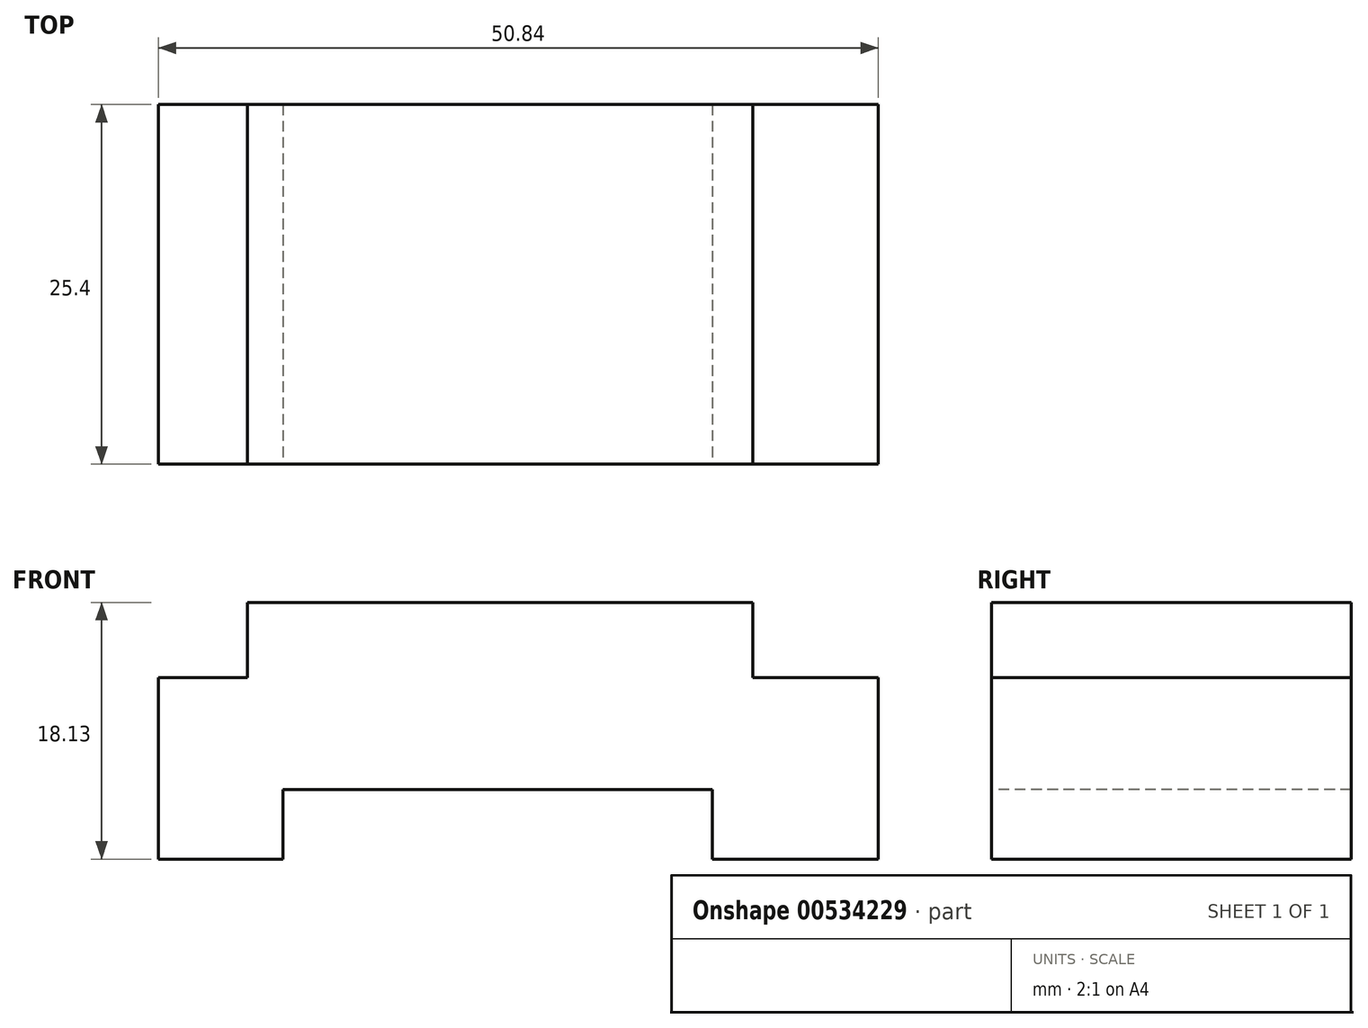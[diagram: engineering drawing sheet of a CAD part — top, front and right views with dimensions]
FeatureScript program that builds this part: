
annotation { "Feature Type Name" : "Feature", "Feature Type Description" : "" }
export const myFeature = defineFeature(function(context is Context, id is Id, definition is map)
    precondition{}
    {
        {
            var Q0;
            Q0=qCreatedBy(makeId("Front.planeOp"),FACE);
            var sketch = newSketch(context, id + "F0", { "sketchPlane" : qUnion([Q0])});
            skLineSegment(sketch, "E0", {"start": v(0, 0) * mm, "end": v(-50.84, 0) * mm});
            skLineSegment(sketch, "E1", {"start": v(-50.84, 0) * mm, "end": v(-50.84, 12.8) * mm});
            skLineSegment(sketch, "E2", {"start": v(-50.84, 12.8) * mm, "end": v(-44.54, 12.8) * mm});
            skLineSegment(sketch, "E3", {"start": v(-44.54, 12.8) * mm, "end": v(-44.54, 18.13) * mm});
            skLineSegment(sketch, "E4", {"start": v(0, 0) * mm, "end": v(0, 12.8) * mm});
            skLineSegment(sketch, "E5", {"start": v(0, 12.8) * mm, "end": v(-8.87, 12.8) * mm});
            skLineSegment(sketch, "E6", {"start": v(-8.87, 12.8) * mm, "end": v(-8.87, 18.13) * mm});
            skLineSegment(sketch, "E7", {"start": v(-8.87, 18.13) * mm, "end": v(-44.54, 18.13) * mm});
            skSolve(sketch);
        }
        {
            var Q0;
            Q0=makeQuery(id+"F0.imprint","IMPRINT",FACE,{"disambiguationData":[TD([[makeQuery(id+"F0.imprint","IMPRINT",EDGE,{"derivedFrom":sQuery(id+"F0.wireOp",EDGE,"E0")}),-1.0]])]});
            extrude(context, id + "F1", {"entities" : qUnion([Q0]), "depth" : 25.4 * mm, "offsetDistance" : 25.4 * mm});
        }
        {
            var Q0;
            Q0=makeQuery(id+"F1.opExtrude","CAP_FACE",FACE,{"disambiguationData":[OSD([sQuery(id+"F0.wireOp",EDGE,"E0"),sQuery(id+"F0.wireOp",EDGE,"E1"),sQuery(id+"F0.wireOp",EDGE,"E2"),sQuery(id+"F0.wireOp",EDGE,"E3"),sQuery(id+"F0.wireOp",EDGE,"E4"),sQuery(id+"F0.wireOp",EDGE,"E5"),sQuery(id+"F0.wireOp",EDGE,"E6"),sQuery(id+"F0.wireOp",EDGE,"E7")])],"isStart":false});
            var sketch = newSketch(context, id + "F2", { "sketchPlane" : qUnion([Q0])});
            skLineSegment(sketch, "E8.bottom", {"start": v(-42.04, 0) * mm, "end": v(-11.72, 0) * mm});
            skLineSegment(sketch, "E8.top", {"start": v(-42.04, 4.92) * mm, "end": v(-11.72, 4.92) * mm});
            skLineSegment(sketch, "E8.left", {"start": v(-42.04, 0) * mm, "end": v(-42.04, 4.92) * mm});
            skLineSegment(sketch, "E8.right", {"start": v(-11.72, 0) * mm, "end": v(-11.72, 4.92) * mm});
            skSolve(sketch);
        }
        {
            var Q0;
            Q0=makeQuery(id+"F2.imprint","IMPRINT",FACE,{"disambiguationData":[TD([[makeQuery(id+"F2.imprint","IMPRINT",EDGE,{"derivedFrom":sQuery(id+"F2.wireOp",EDGE,"E8.bottom")}),-1.0]])]});
            extrude(context, id + "F3", {"entities" : qUnion([Q0]), "operationType" : NewBodyOperationType.REMOVE, "oppositeDirection" : true, "depth" : 25.4 * mm, "offsetDistance" : 25.4 * mm});
        }
    });
